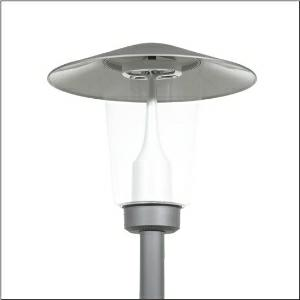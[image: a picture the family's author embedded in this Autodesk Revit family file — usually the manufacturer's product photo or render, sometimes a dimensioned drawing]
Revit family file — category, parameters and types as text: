
# Revit family: pilzleuchte_iq___st1_2a_5xa5235af14h_f6cb
name_source: partatom
category: Lighting Fixtures
units: mm (PartAtom-declared; Revit-internal decimal feet)

## family parameters
Cut with Voids When Loaded = No
Host = Face
Light Source = No
Part Type = Normal
Room Calculation Point = No
Round Connector Dimension = Use Diameter
Shared = No

## types (1)
- --- (1 x LED, 1550 lm, 12.9 W, 2200K)
    Apparent Load = 13 VA
    CIE Flux Codes = 24 61 93 98 100
    Color Rendering = 70
    Color Temperature = 2200K
    Default Elevation = 1800 mm
    Description = Mushroom Luminaire iQ, mast luminaire, Module 540 iQ-SR, primary light control with 3 zone facetted reflector, of plastic, silver coated, highly specular, structured, primary optical cover: cover, of PMMA, transparent, light distribution: ST1.2a, light emission: direct distribution, primary light characteristic: asymmetric, installation type: post-top, LED, High Power LED, rated luminous flux: 1.550lm, luminous efficacy: 120lm/W, light colour: 722, colour temperature: 2200K, control gear: ECG iQ, control: presetting dimming logarithmic, Street-Remote, Auto-Match, Temp-Guard, Lumen-Switch, Night-Set, Smart-Wire, Light-Fading, Desk-Remote (wireless, voltage-free reading and setting of iQ features in the workshop via application-optimized NFC function/RFID function), optimised constant luminous flux control (CLO 2.0), with terminal, 6-pole, max. 2.5mm², mains connection: 220..240V, AC, 50/60Hz, start of lifetime: 13W, end of lifetime: 13W, reduction: 6W, luminaire housing, upper part, of glass-fibre reinforced polyester, coated, Siteco® metallic grey (DB 702S), diameter: 650mm, height: 586mm, spigot size: d x l = 76 x 70mm (post-top) | with reducer (optional accessory) 60 x 70mm, post-top mast mounting element, of diecast aluminium, coated, Siteco® metallic grey (DB 702S), Module 540 iQ-SR, traffic white (RAL 9016), equipment: standard, protection rating (complete): IP65, insulation class (complete): insulation class II (safety insulation), certification: CE, ENEC, VDE, packaging unit: 1 piece

Light Distribution: ST1.2a
    Height = 586 mm
    Lamp = 1 x LED
    Lamp Light Flux = 1550 lm
    Lamp Power = 12.9 W
    Lamp count = 1
    Length = 650 mm
    Luminous efficacy = 120 lm/W
    Manufacturer = Siteco
    ModVariant = No
    Model = 5XA5235AF14H
    Number of Poles = 1
    OnlyDefault = Yes
    Power Factor = 1
    Product Name = Pilzleuchte iQ | ST1.2a
    Product group = mast luminaire | pylon top
    ProductGroupID = 6100
    Protection Class = Protection class II
    Protection Degree = IP 65
    RLX_Detail_Level = 1
    RlxData = <blob elided: 124397 chars, md5=010c54a6>
    Socket = socket
    Standby Power = 0 W
    System Light Flux = 1550 lm
    System Power = 13 W
    Type Comments = factory setting: luminous flux: 100 % | dim-lin: 254 | 516 mA
    Type Image = l_1006077.jpg
    URL = http://relux.com
    VarID = @adj_072043
    Voltage = 0 V
    Weight = 0.00 kg
    Width = 0 mm  [stored 0 ft]

note: [stored X ft] marks values corroborated as IEEE doubles in the binary element streams (Revit-internal decimal feet)

## geometry (parser evidence)
native form markers: Blend x4, Sweep x12
no freeform markers — native parametric forms only
